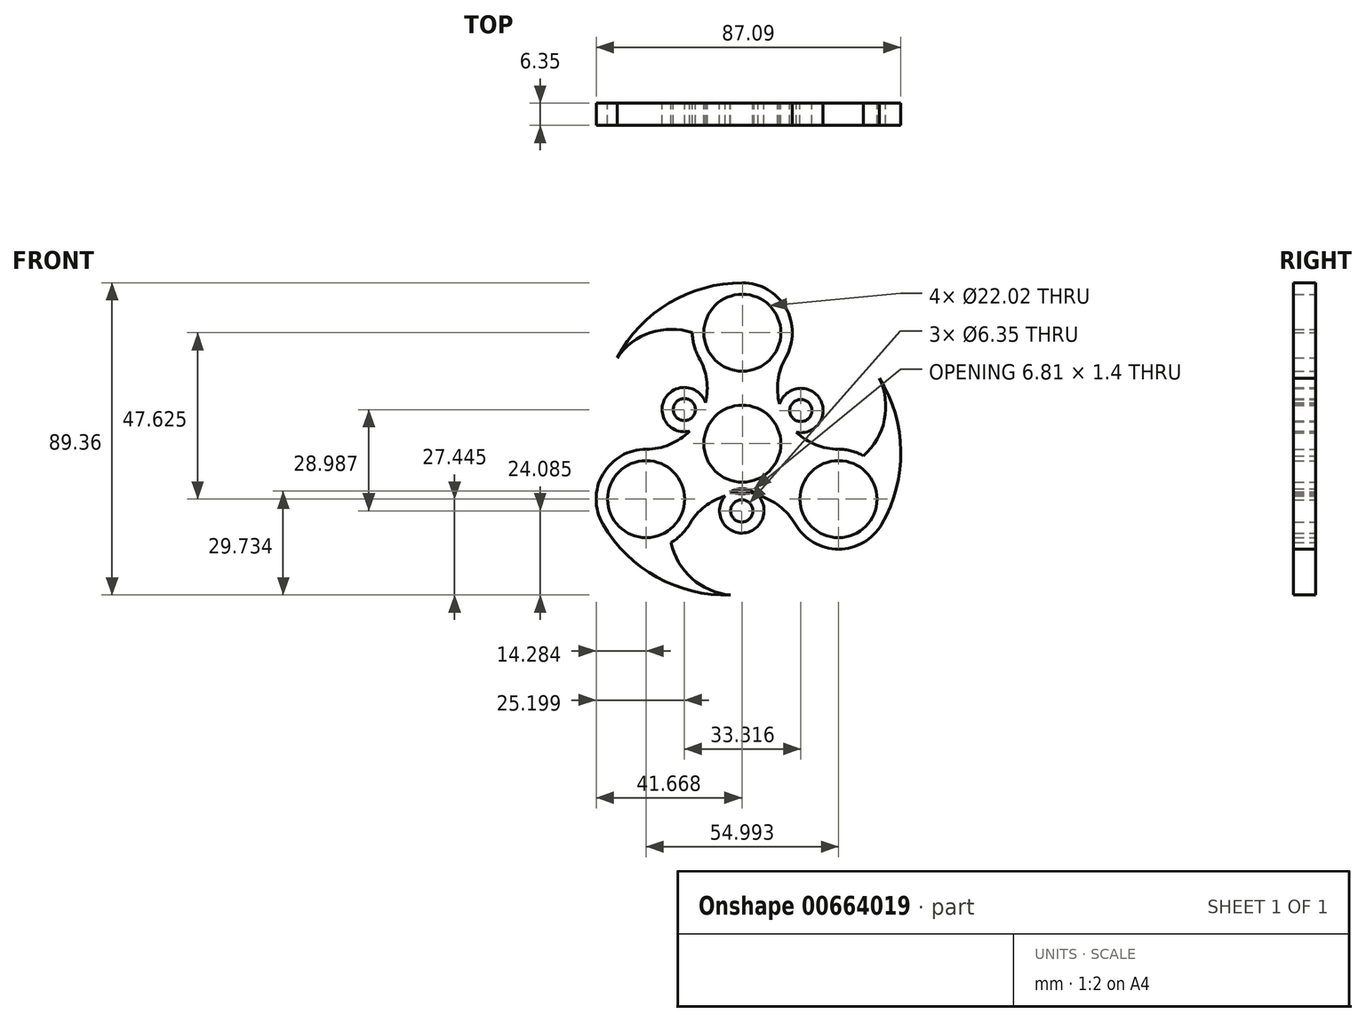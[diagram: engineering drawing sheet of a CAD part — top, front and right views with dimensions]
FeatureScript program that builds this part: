
annotation { "Feature Type Name" : "Feature", "Feature Type Description" : "" }
export const myFeature = defineFeature(function(context is Context, id is Id, definition is map)
    precondition{}
    {
        {
            var Q0;
            Q0=qCreatedBy(makeId("Front.planeOp"),FACE);
            var sketch = newSketch(context, id + "F0", { "sketchPlane" : qUnion([Q0])});
            skCircle(sketch, "E0", {"center": v(0, 31.75) * mm, "radius": 14.29 * mm});
            skCircle(sketch, "E1", {"center": v(0, 31.75) * mm, "radius": 11.01 * mm});
            skCircle(sketch, "E2", {"center": v(0, 0) * mm, "radius": 14.29 * mm});
            skCircle(sketch, "E3", {"center": v(0, 0) * mm, "radius": 11.01 * mm});
            skCircle(sketch, "E4.1.0", {"center": v(-27.5, -15.87) * mm, "radius": 11.01 * mm});
            skCircle(sketch, "E4.1.1", {"center": v(-27.5, -15.87) * mm, "radius": 14.29 * mm});
            skCircle(sketch, "E4.2.0", {"center": v(27.5, -15.88) * mm, "radius": 11.01 * mm});
            skCircle(sketch, "E4.2.1", {"center": v(27.5, -15.88) * mm, "radius": 14.29 * mm});
            skArc(sketch, "E5", {"start": v(-27.5, -1.59) * mm, "mid": v(-12.37, 7.14) * mm, "end": v(-12.37, 24.6) * mm});
            skArc(sketch, "E6.1.0", {"start": v(15.12, -23.02) * mm, "mid": v(0, -14.29) * mm, "end": v(-15.12, -23.02) * mm});
            skArc(sketch, "E6.2.0", {"start": v(12.37, 24.6) * mm, "mid": v(12.37, 7.14) * mm, "end": v(27.5, -1.59) * mm});
            skArc(sketch, "E7", {"start": v(0, 46.04) * mm, "mid": v(-20.86, 40.27) * mm, "end": v(-35.79, 24.6) * mm});
            skArc(sketch, "E8", {"start": v(-14.29, 31.75) * mm, "mid": v(-26.23, 31.76) * mm, "end": v(-35.79, 24.6) * mm});
            skArc(sketch, "E9.1.0", {"start": v(-20.35, -28.25) * mm, "mid": v(-14.39, -38.6) * mm, "end": v(-3.42, -43.3) * mm});
            skArc(sketch, "E9.1.1", {"start": v(-39.87, -23.02) * mm, "mid": v(-24.45, -38.2) * mm, "end": v(-3.42, -43.3) * mm});
            skArc(sketch, "E9.2.0", {"start": v(34.64, -3.5) * mm, "mid": v(40.62, 6.83) * mm, "end": v(39.2, 18.69) * mm});
            skArc(sketch, "E9.2.1", {"start": v(39.87, -23.02) * mm, "mid": v(45.3, -2.07) * mm, "end": v(39.2, 18.69) * mm});
            skCircle(sketch, "E10.2.0", {"center": v(16.74, 9.48) * mm, "radius": 6.35 * mm});
            skCircle(sketch, "E10.2.1", {"center": v(16.74, 9.48) * mm, "radius": 3.18 * mm});
            skCircle(sketch, "E11.1.0", {"center": v(-16.58, 9.75) * mm, "radius": 6.35 * mm});
            skCircle(sketch, "E11.1.1", {"center": v(-16.58, 9.75) * mm, "radius": 3.18 * mm});
            skCircle(sketch, "E11.2.0", {"center": v(-0.15, -19.24) * mm, "radius": 6.35 * mm});
            skCircle(sketch, "E11.2.1", {"center": v(-0.15, -19.24) * mm, "radius": 3.18 * mm});
            skSolve(sketch);
        }
        {
            var Q0;
            Q0=qSketchRegion(id+"F0",true);
            var Q1;
            Q1=makeQuery(id+"F0.imprint","IMPRINT",FACE,{"disambiguationData":[TD([[makeQuery(id+"F0.imprint","IMPRINT",EDGE,{"derivedFrom":sQuery(id+"F0.wireOp",EDGE,"E3")}),-1.0]])]});
            var Q2;
            {var subQ0=sQuery(id+"F0.wireOp",EDGE,"E11.2.0");var subQ1=sQuery(id+"F0.wireOp",EDGE,"E2");var subQ2=makeQuery(id+"F0.imprint","INTERSECT",VERTEX,{"disambiguationData":[OD(0.0)],"derivedFrom":[subQ1,subQ0]});Q2=makeQuery(id+"F0.imprint","IMPRINT",FACE,{"disambiguationData":[TD([[makeQuery(id+"F0.imprint","IMPRINT",EDGE,{"disambiguationData":[TD([[subQ2,-1.0]])],"derivedFrom":subQ1}),1.0]])]});}
            var Q3;
            {var subQ0=sQuery(id+"F0.wireOp",EDGE,"E11.1.0");var subQ1=sQuery(id+"F0.wireOp",EDGE,"E2");var subQ2=makeQuery(id+"F0.imprint","INTERSECT",VERTEX,{"disambiguationData":[OD(0.0)],"derivedFrom":[subQ1,subQ0]});Q3=makeQuery(id+"F0.imprint","IMPRINT",FACE,{"disambiguationData":[TD([[makeQuery(id+"F0.imprint","IMPRINT",EDGE,{"disambiguationData":[TD([[subQ2,-1.0]])],"derivedFrom":subQ1}),1.0]])]});}
            var Q4;
            {var subQ0=sQuery(id+"F0.wireOp",EDGE,"E2");var subQ1=makeQuery(id+"F0.imprint","INTERSECT",VERTEX,{"derivedFrom":[subQ0,sQuery(id+"F0.wireOp",EDGE,"E6.2.0")]});Q4=makeQuery(id+"F0.imprint","IMPRINT",FACE,{"disambiguationData":[TD([[makeQuery(id+"F0.imprint","IMPRINT",EDGE,{"disambiguationData":[TD([[subQ1,1.0]])],"derivedFrom":subQ0}),1.0]])]});}
            extrude(context, id + "F1", {"entities" : qUnion([Q0, Q1, Q2, Q3, Q4]), "depth" : 6.35 * mm, "offsetDistance" : 25.4 * mm});
        }
    });
